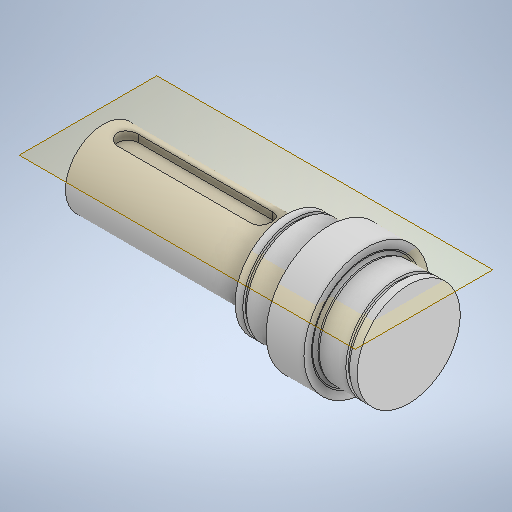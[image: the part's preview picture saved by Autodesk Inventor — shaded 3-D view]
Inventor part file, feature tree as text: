
AUTODESK INVENTOR PART (.ipt)
format: ipt  version: 2025.3 (Build 293356030, 356C)  size: 347,648 bytes
history: native  units: mm
features: sketch x7, revolve x6, plane x1, extrude x1
ambient origin geometry x8: Origin, YZ Plane, XZ Plane, XY Plane, X Axis, Y Axis, Z Axis, Center Point
bodies: Volumenkörper1 (feature_tree)
feature tree (15):
  revolve  "Umdrehung1"
  plane  "Arbeitsebene1"
  extrude  "Extrusion1"  Depth=22.0mm
  revolve  "Umdrehung2"
  revolve  "Umdrehung3"
  revolve  "Umdrehung4"
  revolve  "Umdrehung5"
  revolve  "Umdrehung6"
  sketch  "Skizze1"  dims[d0=0.0mm d1=22.0mm]
  sketch  "Skizze2"  dims[d2=5.0mm d3=0.0mm]
  sketch  "Skizze3"  dims[d4=0.0mm]
  sketch  "Skizze4"  dims[d5=0.0mm]
  sketch  "Skizze5"  dims[d6=0.0mm]
  sketch  "Skizze6"  dims[d7=0.0mm]
  sketch  "Skizze7"  dims[d8=0.0mm]
